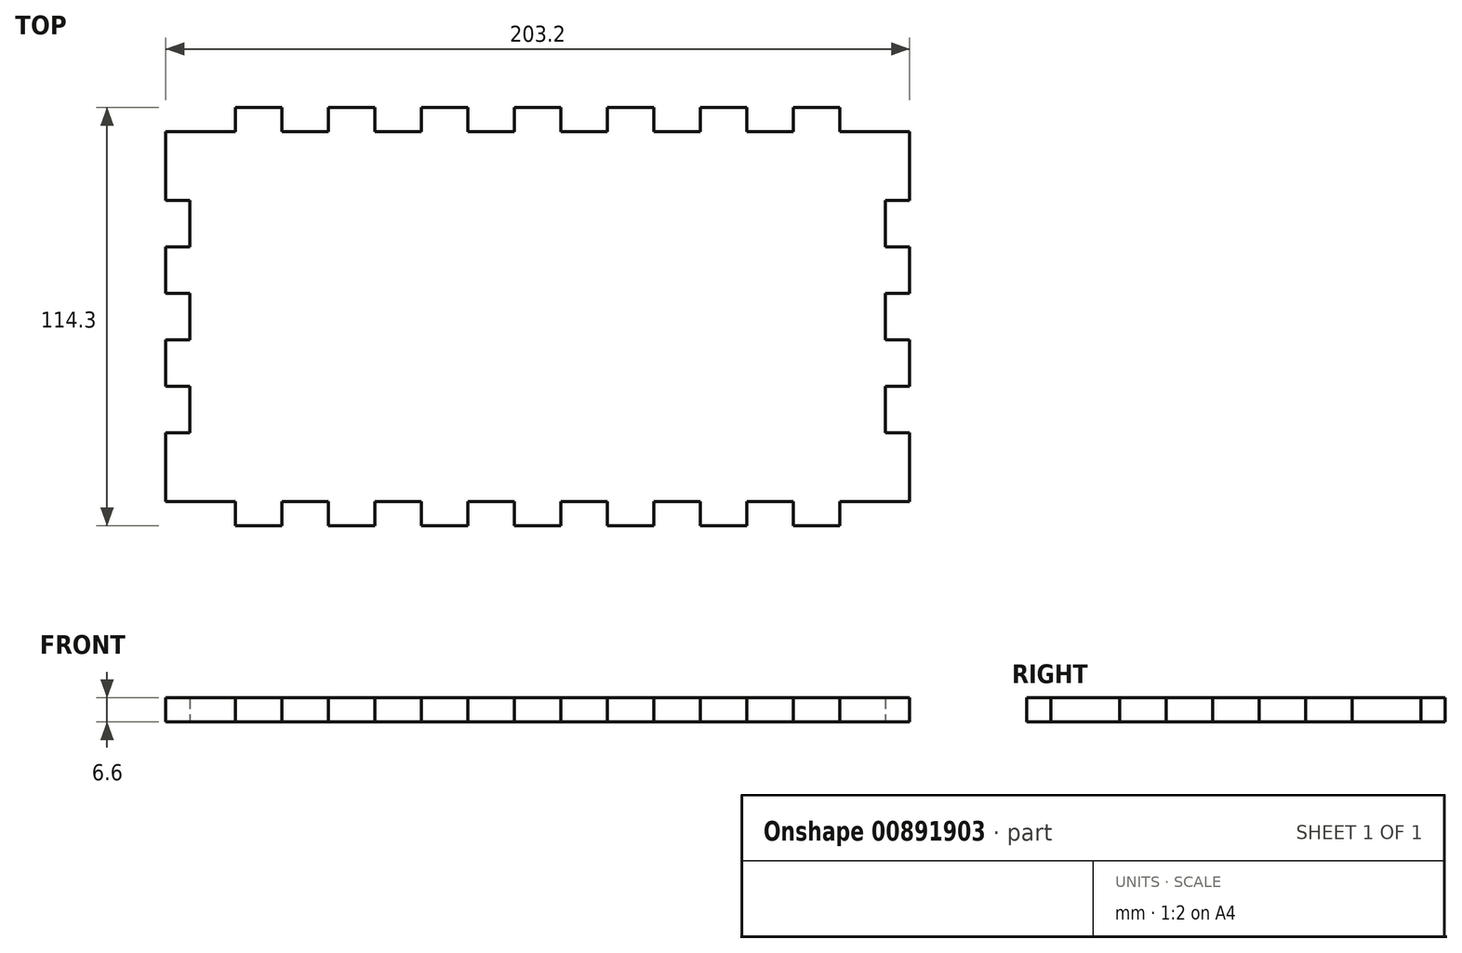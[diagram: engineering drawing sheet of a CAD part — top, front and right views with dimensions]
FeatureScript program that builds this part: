
annotation { "Feature Type Name" : "Feature", "Feature Type Description" : "" }
export const myFeature = defineFeature(function(context is Context, id is Id, definition is map)
    precondition{}
    {
        {
            var Q0;
            Q0=qCreatedBy(makeId("Top.planeOp"),FACE);
            var sketch = newSketch(context, id + "F0", { "sketchPlane" : qUnion([Q0])});
            skLineSegment(sketch, "E0.bottom", {"start": v(19.05, 0) * mm, "end": v(31.75, 0) * mm});
            skLineSegment(sketch, "E0.left", {"start": v(0, -6.6) * mm, "end": v(0, -25.4) * mm});
            skLineSegment(sketch, "E1", {"start": v(0, -6.6) * mm, "end": v(19.05, -6.6) * mm});
            skLineSegment(sketch, "E2", {"start": v(19.05, -6.6) * mm, "end": v(19.05, 0) * mm});
            skLineSegment(sketch, "E3", {"start": v(31.75, 0) * mm, "end": v(31.75, -6.6) * mm});
            skLineSegment(sketch, "E4", {"start": v(31.75, -6.6) * mm, "end": v(44.45, -6.6) * mm});
            skLineSegment(sketch, "E5", {"start": v(44.45, -6.6) * mm, "end": v(44.45, 0) * mm});
            skLineSegment(sketch, "E6", {"start": v(44.45, 0) * mm, "end": v(57.15, 0) * mm});
            skLineSegment(sketch, "E7", {"start": v(57.15, 0) * mm, "end": v(57.15, -6.6) * mm});
            skLineSegment(sketch, "E8", {"start": v(57.15, -6.6) * mm, "end": v(69.85, -6.6) * mm});
            skLineSegment(sketch, "E9", {"start": v(69.85, -6.6) * mm, "end": v(69.85, 0) * mm});
            skPoint(sketch, "E10.orphan", {"position": v(0, 0) * mm});
            skLineSegment(sketch, "E11.trimOffspring", {"start": v(69.85, 0) * mm, "end": v(82.55, 0) * mm});
            skLineSegment(sketch, "E12", {"start": v(82.55, 0) * mm, "end": v(82.55, -6.6) * mm});
            skLineSegment(sketch, "E13", {"start": v(82.55, -6.6) * mm, "end": v(95.25, -6.6) * mm});
            skLineSegment(sketch, "E14", {"start": v(95.25, -6.6) * mm, "end": v(95.25, 0) * mm});
            skLineSegment(sketch, "E15", {"start": v(95.25, 0) * mm, "end": v(107.95, 0) * mm});
            skLineSegment(sketch, "E16", {"start": v(107.95, 0) * mm, "end": v(107.95, -6.6) * mm});
            skLineSegment(sketch, "E17", {"start": v(107.95, -6.6) * mm, "end": v(120.65, -6.6) * mm});
            skLineSegment(sketch, "E18", {"start": v(120.65, -6.6) * mm, "end": v(120.65, 0) * mm});
            skLineSegment(sketch, "E19", {"start": v(120.65, 0) * mm, "end": v(133.35, 0) * mm});
            skLineSegment(sketch, "E20", {"start": v(133.35, 0) * mm, "end": v(133.35, -6.6) * mm});
            skLineSegment(sketch, "E21", {"start": v(133.35, -6.6) * mm, "end": v(146.05, -6.6) * mm});
            skLineSegment(sketch, "E22", {"start": v(146.05, -6.6) * mm, "end": v(146.05, 0) * mm});
            skLineSegment(sketch, "E23.trimOffspring", {"start": v(146.05, 0) * mm, "end": v(158.75, 0) * mm});
            skLineSegment(sketch, "E24", {"start": v(158.75, 0) * mm, "end": v(158.75, -6.6) * mm});
            skLineSegment(sketch, "E25", {"start": v(158.75, -6.6) * mm, "end": v(171.45, -6.6) * mm});
            skLineSegment(sketch, "E26", {"start": v(171.45, -6.6) * mm, "end": v(171.45, 0) * mm});
            skLineSegment(sketch, "E27", {"start": v(171.45, 0) * mm, "end": v(184.15, 0) * mm});
            skLineSegment(sketch, "E28", {"start": v(184.15, 0) * mm, "end": v(184.15, -6.6) * mm});
            skLineSegment(sketch, "E29", {"start": v(184.15, -6.6) * mm, "end": v(203.2, -6.6) * mm});
            skPoint(sketch, "E30.orphan", {"position": v(203.2, 0) * mm});
            skPoint(sketch, "E31.orphan", {"position": v(0, -114.3) * mm});
            skLineSegment(sketch, "E32.MirrorCS", {"start": v(203.2, -6.6) * mm, "end": v(203.2, -25.4) * mm});
            skLineSegment(sketch, "E33", {"start": v(0, -25.4) * mm, "end": v(6.6, -25.4) * mm});
            skLineSegment(sketch, "E34", {"start": v(6.6, -25.4) * mm, "end": v(6.6, -38.1) * mm});
            skLineSegment(sketch, "E35", {"start": v(6.6, -38.1) * mm, "end": v(0, -38.1) * mm});
            skLineSegment(sketch, "E36", {"start": v(0, -38.1) * mm, "end": v(0, -50.8) * mm});
            skLineSegment(sketch, "E37", {"start": v(0, -50.8) * mm, "end": v(6.6, -50.8) * mm});
            skLineSegment(sketch, "E38", {"start": v(6.6, -50.8) * mm, "end": v(6.6, -63.5) * mm});
            skLineSegment(sketch, "E39", {"start": v(6.6, -63.5) * mm, "end": v(0, -63.5) * mm});
            skLineSegment(sketch, "E40", {"start": v(0, -63.5) * mm, "end": v(0, -76.2) * mm});
            skLineSegment(sketch, "E41", {"start": v(0, -76.2) * mm, "end": v(6.6, -76.2) * mm});
            skLineSegment(sketch, "E42", {"start": v(6.6, -76.2) * mm, "end": v(6.6, -88.9) * mm});
            skLineSegment(sketch, "E43", {"start": v(6.6, -88.9) * mm, "end": v(0, -88.9) * mm});
            skLineSegment(sketch, "E44", {"start": v(0, -88.9) * mm, "end": v(0, -107.7) * mm});
            skLineSegment(sketch, "E45", {"start": v(0, -107.7) * mm, "end": v(19.05, -107.7) * mm});
            skLineSegment(sketch, "E46", {"start": v(101.6, 0) * mm, "end": v(101.6, 0) * mm});
            skLineSegment(sketch, "E47.MirrorCS", {"start": v(203.2, -25.4) * mm, "end": v(196.6, -25.4) * mm});
            skLineSegment(sketch, "E48.MirrorCS", {"start": v(196.6, -25.4) * mm, "end": v(196.6, -38.1) * mm});
            skLineSegment(sketch, "E49.MirrorCS", {"start": v(196.6, -38.1) * mm, "end": v(203.2, -38.1) * mm});
            skLineSegment(sketch, "E50.MirrorCS", {"start": v(203.2, -38.1) * mm, "end": v(203.2, -50.8) * mm});
            skLineSegment(sketch, "E51.MirrorCS", {"start": v(196.6, -88.9) * mm, "end": v(203.2, -88.9) * mm});
            skLineSegment(sketch, "E52.MirrorCS", {"start": v(203.2, -50.8) * mm, "end": v(196.6, -50.8) * mm});
            skLineSegment(sketch, "E53.MirrorCS", {"start": v(203.2, -76.2) * mm, "end": v(196.6, -76.2) * mm});
            skLineSegment(sketch, "E54.MirrorCS", {"start": v(196.6, -63.5) * mm, "end": v(203.2, -63.5) * mm});
            skLineSegment(sketch, "E55.MirrorCS", {"start": v(203.2, -107.7) * mm, "end": v(184.15, -107.7) * mm});
            skLineSegment(sketch, "E56.MirrorCS", {"start": v(196.6, -50.8) * mm, "end": v(196.6, -63.5) * mm});
            skLineSegment(sketch, "E57.MirrorCS", {"start": v(203.2, -63.5) * mm, "end": v(203.2, -76.2) * mm});
            skLineSegment(sketch, "E58.MirrorCS", {"start": v(203.2, -88.9) * mm, "end": v(203.2, -107.7) * mm});
            skLineSegment(sketch, "E59.MirrorCS", {"start": v(196.6, -76.2) * mm, "end": v(196.6, -88.9) * mm});
            skPoint(sketch, "E60.MirrorP", {"position": v(203.2, -114.3) * mm});
            skLineSegment(sketch, "E61", {"start": v(6.6, -57.15) * mm, "end": v(6.6, -57.15) * mm});
            skLineSegment(sketch, "E62.MirrorCS", {"start": v(146.05, -107.7) * mm, "end": v(146.05, -114.3) * mm});
            skLineSegment(sketch, "E63.MirrorCS", {"start": v(69.85, -107.7) * mm, "end": v(69.85, -114.3) * mm});
            skLineSegment(sketch, "E64.MirrorCS", {"start": v(31.75, -114.3) * mm, "end": v(31.75, -107.7) * mm});
            skLineSegment(sketch, "E65.MirrorCS", {"start": v(120.65, -107.7) * mm, "end": v(120.65, -114.3) * mm});
            skLineSegment(sketch, "E66.MirrorCS", {"start": v(171.45, -107.7) * mm, "end": v(171.45, -114.3) * mm});
            skLineSegment(sketch, "E67.MirrorCS", {"start": v(82.55, -114.3) * mm, "end": v(82.55, -107.7) * mm});
            skLineSegment(sketch, "E68.MirrorCS", {"start": v(107.95, -114.3) * mm, "end": v(107.95, -107.7) * mm});
            skLineSegment(sketch, "E69.MirrorCS", {"start": v(57.15, -114.3) * mm, "end": v(57.15, -107.7) * mm});
            skLineSegment(sketch, "E70.MirrorCS", {"start": v(133.35, -114.3) * mm, "end": v(133.35, -107.7) * mm});
            skLineSegment(sketch, "E71.MirrorCS", {"start": v(19.05, -107.7) * mm, "end": v(19.05, -114.3) * mm});
            skLineSegment(sketch, "E72.MirrorCS", {"start": v(95.25, -107.7) * mm, "end": v(95.25, -114.3) * mm});
            skLineSegment(sketch, "E73.MirrorCS", {"start": v(158.75, -114.3) * mm, "end": v(158.75, -107.7) * mm});
            skLineSegment(sketch, "E74.MirrorCS", {"start": v(95.25, -114.3) * mm, "end": v(107.95, -114.3) * mm});
            skLineSegment(sketch, "E75.MirrorCS", {"start": v(44.45, -107.7) * mm, "end": v(44.45, -114.3) * mm});
            skLineSegment(sketch, "E76.MirrorCS", {"start": v(184.15, -114.3) * mm, "end": v(184.15, -107.7) * mm});
            skLineSegment(sketch, "E77.MirrorCS", {"start": v(69.85, -114.3) * mm, "end": v(82.55, -114.3) * mm});
            skLineSegment(sketch, "E78.MirrorCS", {"start": v(171.45, -114.3) * mm, "end": v(184.15, -114.3) * mm});
            skLineSegment(sketch, "E79.MirrorCS", {"start": v(19.05, -114.3) * mm, "end": v(31.75, -114.3) * mm});
            skLineSegment(sketch, "E80.MirrorCS", {"start": v(120.65, -114.3) * mm, "end": v(133.35, -114.3) * mm});
            skLineSegment(sketch, "E81.MirrorCS", {"start": v(146.05, -114.3) * mm, "end": v(158.75, -114.3) * mm});
            skLineSegment(sketch, "E82.MirrorCS", {"start": v(44.45, -114.3) * mm, "end": v(57.15, -114.3) * mm});
            skLineSegment(sketch, "E83.MirrorCS", {"start": v(82.55, -107.7) * mm, "end": v(95.25, -107.7) * mm});
            skLineSegment(sketch, "E84.MirrorCS", {"start": v(107.95, -107.7) * mm, "end": v(120.65, -107.7) * mm});
            skLineSegment(sketch, "E85.MirrorCS", {"start": v(31.75, -107.7) * mm, "end": v(44.45, -107.7) * mm});
            skLineSegment(sketch, "E86.MirrorCS", {"start": v(57.15, -107.7) * mm, "end": v(69.85, -107.7) * mm});
            skLineSegment(sketch, "E87.MirrorCS", {"start": v(133.35, -107.7) * mm, "end": v(146.05, -107.7) * mm});
            skLineSegment(sketch, "E88.MirrorCS", {"start": v(158.75, -107.7) * mm, "end": v(171.45, -107.7) * mm});
            skSolve(sketch);
        }
        {
            var Q0;
            Q0=makeQuery(id+"F0.imprint","IMPRINT",FACE,{"disambiguationData":[TD([[makeQuery(id+"F0.imprint","IMPRINT",EDGE,{"derivedFrom":sQuery(id+"F0.wireOp",EDGE,"E1")}),-1.0]])]});
            extrude(context, id + "F1", {"entities" : qUnion([Q0]), "depth" : 6.6 * mm, "offsetDistance" : 25.4 * mm});
        }
    });
